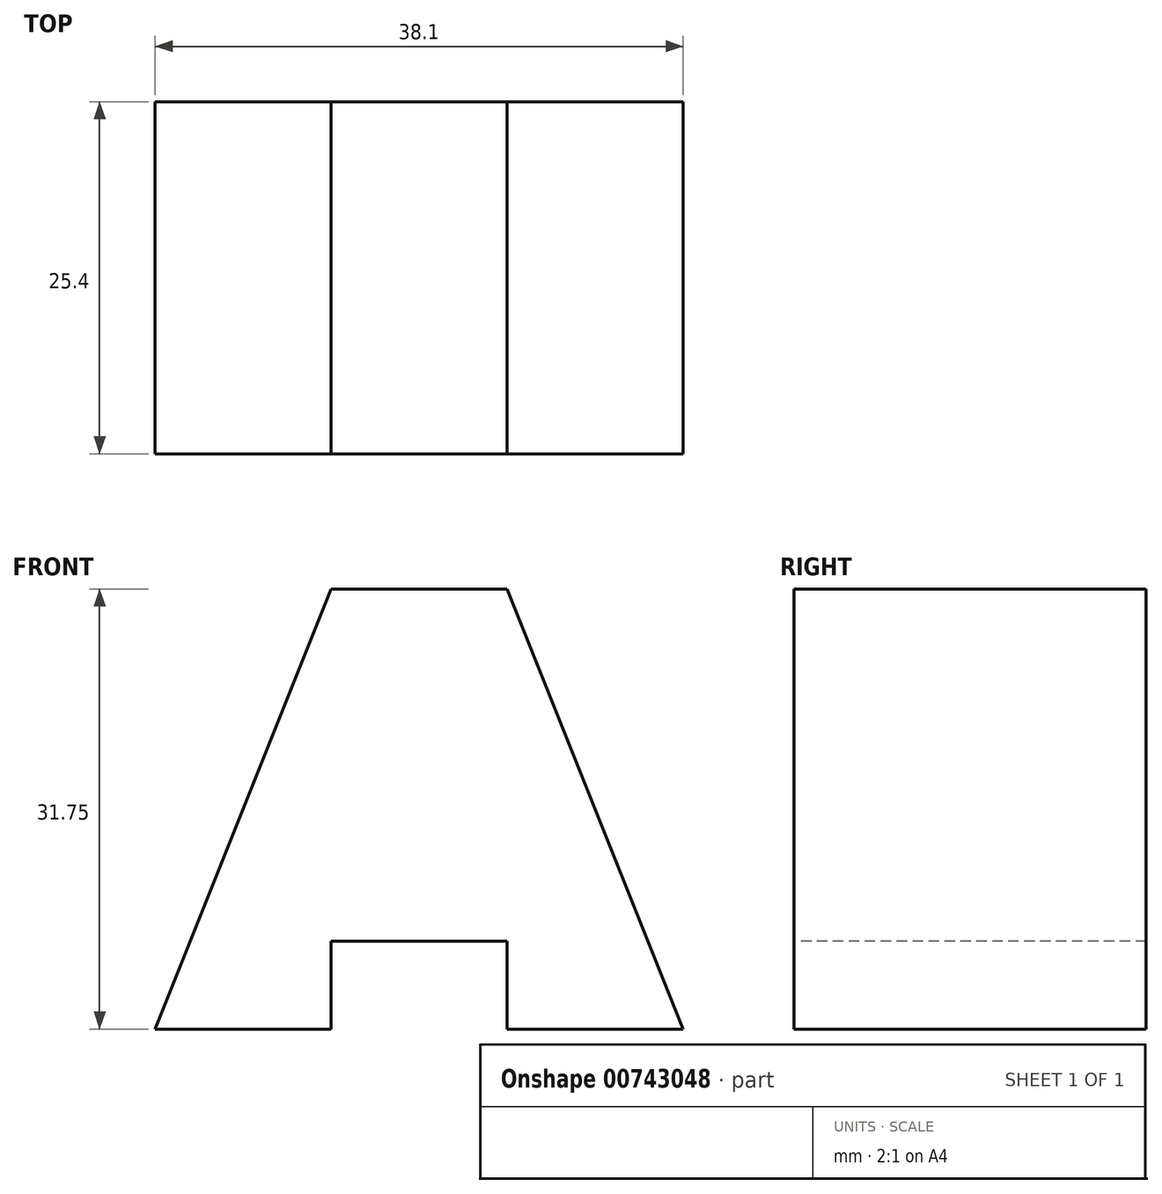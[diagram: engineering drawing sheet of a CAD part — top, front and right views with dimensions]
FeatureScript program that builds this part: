
annotation { "Feature Type Name" : "Feature", "Feature Type Description" : "" }
export const myFeature = defineFeature(function(context is Context, id is Id, definition is map)
    precondition{}
    {
        {
            var Q0;
            Q0=qCreatedBy(makeId("Front.planeOp"),FACE);
            var sketch = newSketch(context, id + "F0", { "sketchPlane" : qUnion([Q0])});
            skLineSegment(sketch, "E0", {"start": v(0, 0) * mm, "end": v(38.1, 0) * mm});
            skLineSegment(sketch, "E1", {"start": v(38.1, 0) * mm, "end": v(38.1, 31.75) * mm});
            skLineSegment(sketch, "E2", {"start": v(38.1, 31.75) * mm, "end": v(0, 31.75) * mm});
            skLineSegment(sketch, "E3", {"start": v(0, 31.75) * mm, "end": v(0, 0) * mm});
            skSolve(sketch);
        }
        {
            var Q0;
            Q0=makeQuery(id+"F0.imprint","IMPRINT",FACE,{"disambiguationData":[TD([[makeQuery(id+"F0.imprint","IMPRINT",EDGE,{"derivedFrom":sQuery(id+"F0.wireOp",EDGE,"E0")}),1.0]])]});
            extrude(context, id + "F1", {"entities" : qUnion([Q0]), "oppositeDirection" : true, "depth" : 25.4 * mm, "offsetDistance" : 25.4 * mm});
        }
        {
            var Q0;
            Q0=makeQuery(id+"F1.opExtrude","CAP_FACE",FACE,{"disambiguationData":[OSD([sQuery(id+"F0.wireOp",EDGE,"E0"),sQuery(id+"F0.wireOp",EDGE,"E1"),sQuery(id+"F0.wireOp",EDGE,"E2"),sQuery(id+"F0.wireOp",EDGE,"E3")])],"isStart":true});
            var sketch = newSketch(context, id + "F2", { "sketchPlane" : qUnion([Q0])});
            skLineSegment(sketch, "E4", {"start": v(12.7, 0) * mm, "end": v(12.7, 6.35) * mm});
            skLineSegment(sketch, "E5", {"start": v(12.7, 6.35) * mm, "end": v(25.4, 6.35) * mm});
            skLineSegment(sketch, "E6", {"start": v(25.4, 6.35) * mm, "end": v(25.4, 0) * mm});
            skLineSegment(sketch, "E7", {"start": v(25.4, 0) * mm, "end": v(12.7, 0) * mm});
            skSolve(sketch);
        }
        {
            var Q0;
            Q0=makeQuery(id+"F2.imprint","IMPRINT",FACE,{"disambiguationData":[TD([[makeQuery(id+"F2.imprint","IMPRINT",EDGE,{"derivedFrom":sQuery(id+"F2.wireOp",EDGE,"E4")}),-1.0]])]});
            extrude(context, id + "F3", {"entities" : qUnion([Q0]), "operationType" : NewBodyOperationType.REMOVE, "oppositeDirection" : true, "depth" : 25.4 * mm, "offsetDistance" : 25.4 * mm});
        }
        {
            var Q0;
            Q0=makeQuery(id+"F1.opExtrude","CAP_FACE",FACE,{"disambiguationData":[OSD([sQuery(id+"F0.wireOp",EDGE,"E0"),sQuery(id+"F0.wireOp",EDGE,"E1"),sQuery(id+"F0.wireOp",EDGE,"E2"),sQuery(id+"F0.wireOp",EDGE,"E3")])],"isStart":true});
            var sketch = newSketch(context, id + "F4", { "sketchPlane" : qUnion([Q0])});
            skLineSegment(sketch, "E8", {"start": v(38.1, 0) * mm, "end": v(38.1, 31.75) * mm});
            skLineSegment(sketch, "E9", {"start": v(38.1, 31.75) * mm, "end": v(25.4, 31.75) * mm});
            skLineSegment(sketch, "E10", {"start": v(25.4, 31.75) * mm, "end": v(38.1, 0) * mm});
            skSolve(sketch);
        }
        {
            var Q0;
            Q0=makeQuery(id+"F4.imprint","IMPRINT",FACE,{"disambiguationData":[TD([[makeQuery(id+"F4.imprint","IMPRINT",EDGE,{"derivedFrom":sQuery(id+"F4.wireOp",EDGE,"E8")}),1.0]])]});
            extrude(context, id + "F5", {"entities" : qUnion([Q0]), "operationType" : NewBodyOperationType.REMOVE, "oppositeDirection" : true, "depth" : 25.4 * mm, "offsetDistance" : 25.4 * mm});
        }
        {
            var Q0;
            Q0=makeQuery(id+"F1.opExtrude","CAP_FACE",FACE,{"disambiguationData":[OSD([sQuery(id+"F0.wireOp",EDGE,"E0"),sQuery(id+"F0.wireOp",EDGE,"E1"),sQuery(id+"F0.wireOp",EDGE,"E2"),sQuery(id+"F0.wireOp",EDGE,"E3")])],"isStart":true});
            var sketch = newSketch(context, id + "F6", { "sketchPlane" : qUnion([Q0])});
            skLineSegment(sketch, "E11", {"start": v(0, 0) * mm, "end": v(0, 31.75) * mm});
            skLineSegment(sketch, "E12", {"start": v(0, 31.75) * mm, "end": v(12.7, 31.75) * mm});
            skLineSegment(sketch, "E13", {"start": v(12.7, 31.75) * mm, "end": v(0, 0) * mm});
            skSolve(sketch);
        }
        {
            var Q0;
            Q0=makeQuery(id+"F6.imprint","IMPRINT",FACE,{"disambiguationData":[TD([[makeQuery(id+"F6.imprint","IMPRINT",EDGE,{"derivedFrom":sQuery(id+"F6.wireOp",EDGE,"E11")}),1.0]])]});
            extrude(context, id + "F7", {"entities" : qUnion([Q0]), "operationType" : NewBodyOperationType.REMOVE, "oppositeDirection" : true, "depth" : 25.4 * mm, "offsetDistance" : 25.4 * mm});
        }
    });
